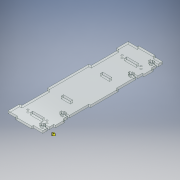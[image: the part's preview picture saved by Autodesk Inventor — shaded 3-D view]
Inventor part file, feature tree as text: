
AUTODESK INVENTOR PART (.ipt)
format: ipt  version: 2019 (Build 230136000, 136)  size: 484,864 bytes
history: native  units: mm
features: extrude x8, sketch x8, projected_geometry x7
ambient origin geometry x8: Origin, YZ Plane, XZ Plane, XY Plane, X Axis, Y Axis, Z Axis, Center Point
bodies: Solid1 (feature_tree)
feature tree (23):
  extrude  "Extrusion1"  Depth=5.0mm TaperAngle=0.0deg
  extrude  "Extrusion2"  Depth=5.0mm
  extrude  "Extrusion3"  Depth=60.0mm
  extrude  "Extrusion4"  Depth=75.0mm
  extrude  "Extrusion5"  Depth=20.0mm
  extrude  "Extrusion6"  Depth=25.0mm
  extrude  "Extrusion7"  Depth=22.5mm
  extrude  "Extrusion8"  Depth=5.0mm TaperAngle=0.0deg
  sketch  "Sketch1"  dims[d1=300.0mm d6=5.0mm d7=0.0mm]
  sketch  "Sketch2"  dims[d8=5.0mm d10=5.0mm]
  projected_geometry  "Projected Loop1"
  sketch  "Sketch3"  dims[d11=45.0mm d13=60.0mm]
  projected_geometry  "Projected Loop2"
  sketch  "Sketch4"  dims[d14=75.0mm d15=75.0mm]
  projected_geometry  "Projected Loop3"
  sketch  "Sketch5"  dims[d16=20.0mm d17=20.0mm]
  projected_geometry  "Projected Loop4"
  sketch  "Sketch6"  dims[d18=5.0mm d19=0.0mm d20=25.0mm]
  projected_geometry  "Projected Loop5"
  sketch  "Sketch8"  dims[d21=5.0mm d22=22.5mm]
  projected_geometry  "Projected Loop6"
  sketch  "Sketch9"  dims[d23=35.0mm d24=5.0mm d25=0.0mm d26=5.0mm d27=25.0mm d28=26.0mm d29=90.0mm d30=45.0mm d31=60.0mm d32=22.5mm d33=4.0mm d34=4.0mm d35=4.0mm d36=4.0mm d37=8.0mm d38=8.0mm d39=8.0mm d40=8.0mm d41=5.0mm d42=0.0mm d43=20.0mm d44=5.0mm d45=25.0mm d46=10.0mm d47=0.0mm d48=15.0mm d49=4.0mm d50=4.0mm d51=8.0mm d52=4.0mm d53=10.0mm d54=15.0mm d55=4.0mm d56=4.0mm d57=8.0mm d58=4.0mm d60=40.0mm d61=3.5mm d62=20.0mm d63=10.0mm d64=15.0mm d65=4.0mm d66=4.0mm d67=8.0mm d68=4.0mm d69=15.0mm d70=4.0mm d71=4.0mm d72=8.0mm d73=4.0mm d74=40.0mm d75=3.5mm d76=20.0mm d77=10.0mm d78=10.0mm d79=3.5mm d80=60.0mm d81=30.0mm d82=5.0mm d83=0.0mm d152=17.0mm d153=4.0mm d154=4.0mm d155=8.0mm d156=10.0mm d157=17.0mm d158=4.0mm d159=4.0mm d160=8.0mm d161=17.0mm d162=4.0mm d163=4.0mm d164=8.0mm d165=17.0mm d166=4.0mm d167=4.0mm d168=8.0mm d169=10.0mm d170=10.0mm d171=10.0mm d172=10.0mm d173=0.0mm d174=35.0mm d175=3.5mm d176=35.0mm d177=3.5mm d178=20.0mm d179=20.0mm d180=5.0mm d181=0.0mm d182=4.0mm d183=0.0mm d184=4.0mm d185=0.0mm d186=4.0mm d187=0.0mm d188=4.0mm]
  projected_geometry  "Projected Loop7"
